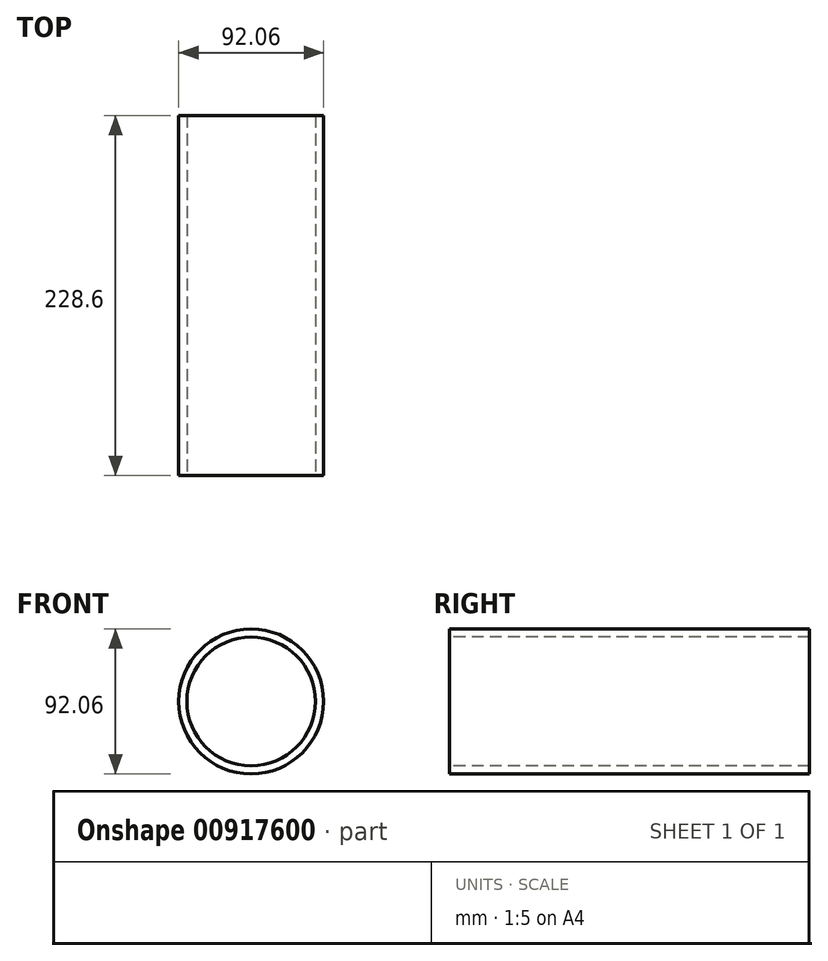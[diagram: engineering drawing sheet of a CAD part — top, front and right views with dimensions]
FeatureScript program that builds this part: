
annotation { "Feature Type Name" : "Feature", "Feature Type Description" : "" }
export const myFeature = defineFeature(function(context is Context, id is Id, definition is map)
    precondition{}
    {
        {
            var Q0;
            Q0=qCreatedBy(makeId("Front.planeOp"),FACE);
            var sketch = newSketch(context, id + "F0", { "sketchPlane" : qUnion([Q0])});
            skCircle(sketch, "E0", {"center": v(0, 0) * mm, "radius": 46.03 * mm});
            skCircle(sketch, "E1", {"center": v(0, 0) * mm, "radius": 40.85 * mm});
            skSolve(sketch);
        }
        {
            var Q0;
            Q0=sQuery(id+"F0.wireOp",EDGE,"E0");
            var Q1;
            Q1=sQuery(id+"F0.wireOp",EDGE,"E1");
            extrude(context, id + "F1", {"bodyType" : ToolBodyType.SURFACE, "surfaceEntities" : qUnion([Q0, Q1]), "depth" : 228.6 * mm, "offsetDistance" : 25.4 * mm});
        }
    });
